FCSTD DOCUMENT  (FreeCAD 0.19R16699 (Git))
Label: RD901F Series Spreadsheet
License: All rights reserved
LicenseURL: http://en.wikipedia.org/wiki/All_rights_reserved
objects: Spreadsheet::Sheet×1, Sketcher::SketchObject×1, PartDesign::Body×1
note: 2 computed .brp shape members not serialized (recipe doc carries the construction recipe); baked Part::Feature solids carry a one-line shape summary decoded from their .brp

FEATURE [Spreadsheet::Sheet] Spreadsheet  label="dims"
  cells = A1=bodyx; B1(bodyx)==9.5mm; C1=width of the body in x direction; A2=bodyy1; B2(bodyy1)==4.85mm; C2=width of the body in y direction, above x axis; A3=bodyy2; B3(bodyy2)==6.5mm; C3=width of the body in y direction, below x-axis; A4=bodyz1; B4(bodyz1)==0.75mm; C4=height of the body in z direction, bottom part; A5=bodyz2; B5(bodyz2)==5mm; C5=height of the body in z direction, mid part; A6=bodyz3; B6(bodyz3)==1.25mm; C6=height of the body in z direction, top part; A7=rivetcutbottomrightx; B7(rivetcutbottomrightx)==1.5mm; A8=rivetcutbottomrighty; B8(rivetcutbottomrighty)==2mm; A9=rivetcutbottomrightz; B9(rivetcutbottomrightz)==0.5mm; A10=rivetcutbottomrightr; B10(rivetcutbottomrightr)==0.75mm; A11=rivetcutbottomleftx; B11(rivetcutbottomleftx)==1.5mm; A12=rivetcutbottomlefty; B12(rivetcutbottomlefty)==2mm; A13=rivetcutbottomleftz; B13(rivetcutbottomleftz)==0.5mm; A14=rivetcutbottomleftr; B14(rivetcutbottomleftr)==0.75mm; A16=rivet-bottom-radius; B16==0.75mm; A17=rivet-bottom-x; A18=rivet-bottom-y; A19=rivet-top-radius-outer; B19==0.75mm; A20=rivet-top-radius-inner; B20==0.5mm; A21=rivet-top-depth; A24=cutout-depth; B24==0.75mm
FEATURE [Sketcher::SketchObject] Sketch
  MapMode = 5
  Support = -> [XY_Plane]
  expr: Constraints[23] = dims.bodyx
  sketch-geometry (12):
    g0: LineSegment StartX=-4.75 StartY=2.41742 StartZ=0 EndX=0.560841 EndY=2.41742 EndZ=0
    g1: LineSegment StartX=0.560841 StartY=2.41742 StartZ=0 EndX=0.560841 EndY=0.877383 EndZ=0
    g2: ArcOfCircle CenterX=0.630189 CenterY=0.877383 CenterZ=0 NormalX=0 NormalY=0 NormalZ=1 AngleXU=0 Radius=0.0693476 StartAngle=3.14159 EndAngle=4.71239
    g3: LineSegment StartX=0.630189 StartY=0.808035 StartZ=0 EndX=4.75 EndY=0.808035 EndZ=0
    g4: LineSegment StartX=4.75 StartY=0.808035 StartZ=0 EndX=4.75 EndY=0 EndZ=0
    g5: LineSegment StartX=4.75 StartY=0 StartZ=0 EndX=4.75 EndY=-2.74907 EndZ=0
    g6: LineSegment StartX=4.75 StartY=-2.74907 StartZ=0 EndX=-4.75 EndY=-2.74907 EndZ=0
    g7: LineSegment StartX=-4.75 StartY=-2.74907 StartZ=0 EndX=-4.75 EndY=-1.46556 EndZ=0
    g8: LineSegment StartX=-4.75 StartY=-1.46556 StartZ=0 EndX=-3.89031 EndY=-1.46556 EndZ=0
    g9: ArcOfCircle CenterX=-3.89031 CenterY=-0.900912 CenterZ=0 NormalX=0 NormalY=0 NormalZ=1 AngleXU=0 Radius=0.564645 StartAngle=4.71239 EndAngle=7.2285
    g10: LineSegment StartX=-3.82674 StartY=0 StartZ=0 EndX=-4.75 EndY=0 EndZ=0
    g11: LineSegment StartX=-4.75 StartY=0 StartZ=0 EndX=-4.75 EndY=2.41742 EndZ=0
  constraints (24):
    c: Horizontal(g0)
    c: Coincident(g0,g1)
    c: Vertical(g1)
    c: Tangent(g1,g2) = -1.5708
    c: Tangent(g2,g3) = -1.5708
    c: Coincident(g3,g4)
    c: PointOnObject(g4,g-1)
    c: Vertical(g4)
    c: Coincident(g4,g5)
    c: Vertical(g5)
    c: Coincident(g5,g6)
    c: Coincident(g6,g7)
    c: Vertical(g7)
    c: Coincident(g7,g8)
    c: Horizontal(g8)
    c: Tangent(g8,g9) = -1.5708
    c: Coincident(g10,g11)
    c: Coincident(g11,g0)
    c: Vertical(g11)
    c: Horizontal(g10)
    c: Symmetric(g5,g6,g-2)
    c: Horizontal(g3)
    c: Symmetric(g4,g10,g-2)
    c: DistanceX(g6,g5) = 9.5
FEATURE [PartDesign::Body] Body
  Group = -> [Sketch]
  Origin = -> Origin
